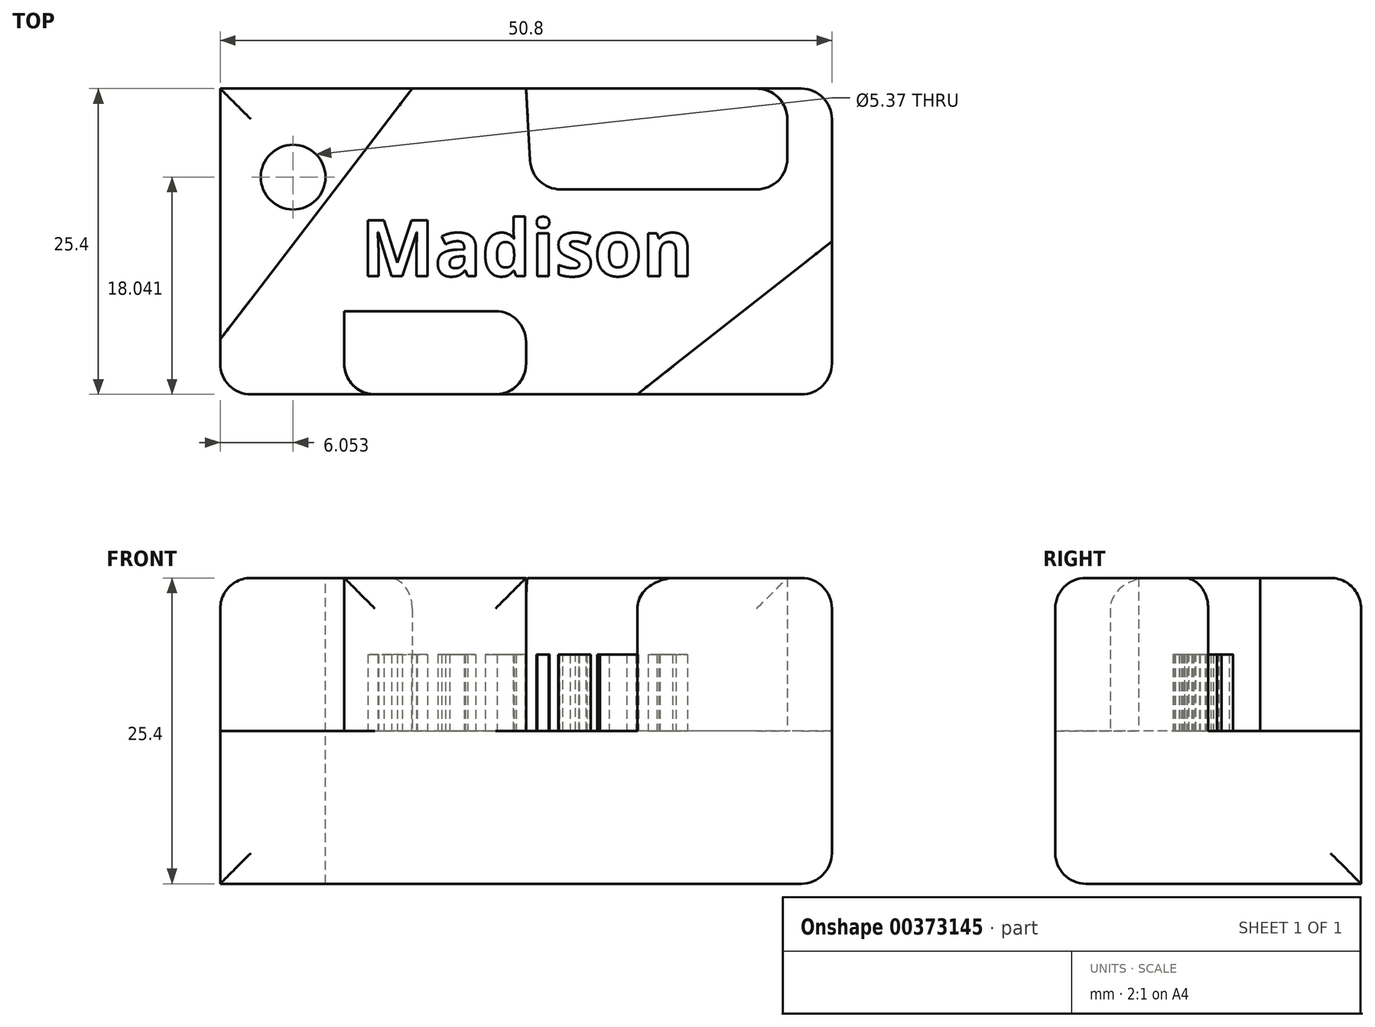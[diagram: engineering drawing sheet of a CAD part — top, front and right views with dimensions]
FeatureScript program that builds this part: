
annotation { "Feature Type Name" : "Feature", "Feature Type Description" : "" }
export const myFeature = defineFeature(function(context is Context, id is Id, definition is map)
    precondition{}
    {
        {
            var Q0;
            Q0=qCreatedBy(makeId("Front.planeOp"),FACE);
            var sketch = newSketch(context, id + "F0", { "sketchPlane" : qUnion([Q0])});
            skLineSegment(sketch, "E0", {"start": v(0, 12.7) * mm, "end": v(0, 0) * mm});
            skLineSegment(sketch, "E1", {"start": v(0, 0) * mm, "end": v(50.8, 0) * mm});
            skLineSegment(sketch, "E2", {"start": v(50.8, 0) * mm, "end": v(50.8, 12.7) * mm});
            skLineSegment(sketch, "E3", {"start": v(50.8, 12.7) * mm, "end": v(0, 12.7) * mm});
            skSolve(sketch);
        }
        {
            var Q0;
            Q0 = qSketchRegion(id + "F0", true);
            extrude(context, id + "F1", {"entities" : qUnion([Q0]), "depth" : 25.4 * mm});
        }
        {
            var Q0;
            Q0=makeQuery(id+"F1.opExtrude","SWEPT_FACE",FACE,{"disambiguationData":[OSD([sQuery(id+"F0.wireOp",EDGE,"E3")])]});
            var sketch = newSketch(context, id + "F2", { "sketchPlane" : qUnion([Q0])});
            skLineSegment(sketch, "E4", {"start": v(0, -20.83) * mm, "end": v(0, 0) * mm});
            skLineSegment(sketch, "E5", {"start": v(0, 0) * mm, "end": v(15.94, 0) * mm});
            skLineSegment(sketch, "E6", {"start": v(15.94, 0) * mm, "end": v(0, -20.83) * mm});
            skLineSegment(sketch, "E7", {"start": v(25.4, 0) * mm, "end": v(47.1, 0) * mm});
            skLineSegment(sketch, "E8", {"start": v(47.1, 0) * mm, "end": v(47.1, -8.37) * mm});
            skLineSegment(sketch, "E9", {"start": v(47.1, -8.37) * mm, "end": v(25.87, -8.37) * mm});
            skLineSegment(sketch, "E10", {"start": v(25.87, -8.37) * mm, "end": v(25.4, 0) * mm});
            skLineSegment(sketch, "E11", {"start": v(34.63, -25.4) * mm, "end": v(50.8, -25.4) * mm});
            skLineSegment(sketch, "E12", {"start": v(50.8, -25.4) * mm, "end": v(50.8, -12.7) * mm});
            skLineSegment(sketch, "E13", {"start": v(50.8, -12.7) * mm, "end": v(34.63, -25.4) * mm});
            skLineSegment(sketch, "E14", {"start": v(10.3, -25.4) * mm, "end": v(10.3, -18.5) * mm});
            skLineSegment(sketch, "E15", {"start": v(10.3, -18.5) * mm, "end": v(25.4, -18.5) * mm});
            skLineSegment(sketch, "E16", {"start": v(25.4, -18.5) * mm, "end": v(25.4, -25.4) * mm});
            skLineSegment(sketch, "E17", {"start": v(25.4, -25.4) * mm, "end": v(10.3, -25.4) * mm});
            skSolve(sketch);
        }
        {
            var Q0;
            Q0 = qSketchRegion(id + "F2", true);
            extrude(context, id + "F3", {"entities" : qUnion([Q0]), "operationType" : NewBodyOperationType.ADD, "depth" : 12.7 * mm});
        }
        {
            var Q0;
            Q0=makeQuery(id+"F3.opExtrude","CAP_EDGE",EDGE,{"disambiguationData":[OSD([sQuery(id+"F2.wireOp",EDGE,"E4")])],"isStart":false});
            var Q1;
            Q1=makeQuery(id+"F3.opExtrude","CAP_EDGE",EDGE,{"disambiguationData":[OSD([sQuery(id+"F2.wireOp",EDGE,"E5")])],"isStart":false});
            var Q2;
            Q2=makeQuery(id+"F3.opExtrude","CAP_EDGE",EDGE,{"disambiguationData":[OSD([sQuery(id+"F2.wireOp",EDGE,"E7")])],"isStart":false});
            var Q3;
            Q3=makeQuery(id+"F3.opExtrude","CAP_EDGE",EDGE,{"disambiguationData":[OSD([sQuery(id+"F2.wireOp",EDGE,"E17")])],"isStart":false});
            var Q4;
            Q4=makeQuery(id+"F3.opExtrude","CAP_EDGE",EDGE,{"disambiguationData":[OSD([sQuery(id+"F2.wireOp",EDGE,"E11")])],"isStart":false});
            var Q5;
            Q5=makeQuery(id+"F3.opExtrude","CAP_EDGE",EDGE,{"disambiguationData":[OSD([sQuery(id+"F2.wireOp",EDGE,"E12")])],"isStart":false});
            var Q6;
            Q6=makeQuery(id+"F1.opExtrude","SWEPT_EDGE",EDGE,{"disambiguationData":[OSD([sQuery(id+"F0.wireOp",EDGE,"E1"),sQuery(id+"F0.wireOp",EDGE,"E2")])]});
            var Q7;
            Q7=makeQuery(id+"F1.opExtrude","CAP_EDGE",EDGE,{"disambiguationData":[OSD([sQuery(id+"F0.wireOp",EDGE,"E1")])],"isStart":false});
            var Q8;
            Q8=makeQuery(id+"F3.boolean.opBoolean","MERGE",EDGE,{"derivedFrom":[makeQuery(id+"F1.opExtrude","CAP_EDGE",EDGE,{"disambiguationData":[OSD([sQuery(id+"F0.wireOp",EDGE,"E2")])],"isStart":false}),makeQuery(id+"F3.opExtrude","SWEPT_EDGE",EDGE,{"disambiguationData":[OSD([sQuery(id+"F2.wireOp",EDGE,"E11"),sQuery(id+"F2.wireOp",EDGE,"E12")])]})]});
            var Q9;
            Q9=makeQuery(id+"F1.opExtrude","CAP_EDGE",EDGE,{"disambiguationData":[OSD([sQuery(id+"F0.wireOp",EDGE,"E2")])],"isStart":true});
            var Q10;
            Q10=makeQuery(id+"F1.opExtrude","CAP_EDGE",EDGE,{"disambiguationData":[OSD([sQuery(id+"F0.wireOp",EDGE,"E0")])],"isStart":false});
            var Q11;
            Q11=makeQuery(id+"F3.opExtrude","SWEPT_EDGE",EDGE,{"disambiguationData":[OSD([sQuery(id+"F0.wireOp",EDGE,"E3"),sQuery(id+"F2.wireOp",EDGE,"E7"),sQuery(id+"F2.wireOp",EDGE,"E8")])]});
            var Q12;
            Q12=makeQuery(id+"F3.opExtrude","SWEPT_EDGE",EDGE,{"disambiguationData":[OSD([sQuery(id+"F0.wireOp",EDGE,"E3"),sQuery(id+"F2.wireOp",EDGE,"E16"),sQuery(id+"F2.wireOp",EDGE,"E17")])]});
            var Q13;
            Q13=makeQuery(id+"F3.opExtrude","SWEPT_EDGE",EDGE,{"disambiguationData":[OSD([sQuery(id+"F0.wireOp",EDGE,"E3"),sQuery(id+"F2.wireOp",EDGE,"E14"),sQuery(id+"F2.wireOp",EDGE,"E17")])]});
            var Q14;
            Q14=makeQuery(id+"F3.opExtrude","SWEPT_EDGE",EDGE,{"disambiguationData":[OSD([sQuery(id+"F2.wireOp",EDGE,"E8"),sQuery(id+"F2.wireOp",EDGE,"E9")])]});
            var Q15;
            Q15=makeQuery(id+"F3.opExtrude","SWEPT_EDGE",EDGE,{"disambiguationData":[OSD([sQuery(id+"F2.wireOp",EDGE,"E9"),sQuery(id+"F2.wireOp",EDGE,"E10")])]});
            var Q16;
            Q16=makeQuery(id+"F3.opExtrude","SWEPT_EDGE",EDGE,{"disambiguationData":[OSD([sQuery(id+"F2.wireOp",EDGE,"E15"),sQuery(id+"F2.wireOp",EDGE,"E16")])]});
            fillet(context, id + "F4", {"entities" : qUnion([Q0, Q1, Q2, Q3, Q4, Q5, Q6, Q7, Q8, Q9, Q10, Q11, Q12, Q13, Q14, Q15, Q16]), "radius" : 2.54 * mm, "tangentPropagation" : true, "allowEdgeOverflow" : false});
        }
        {
            var Q0;
            Q0=makeQuery(id+"F1.opExtrude","SWEPT_FACE",FACE,{"disambiguationData":[OSD([sQuery(id+"F0.wireOp",EDGE,"E3")])]});
            var sketch = newSketch(context, id + "F5", { "sketchPlane" : qUnion([Q0])});
            skText(sketch, "E18", { "text": "Madison", "fontName": "OpenSans-Bold.ttf"});
            const initialGuessF5  = {"E18": [0.01168, -0.01557, 1, 0, 0.00467]};
            skSetInitialGuess(sketch, initialGuessF5);
            skSolve(sketch);
        }
        {
            var Q0;
            Q0 = qSketchRegion(id + "F5", true);
            extrude(context, id + "F6", {"entities" : qUnion([Q0]), "operationType" : NewBodyOperationType.ADD, "depth" : 6.35 * mm});
        }
        {
            var Q0;
            Q0=makeQuery(id+"F3.opExtrude","CAP_FACE",FACE,{"disambiguationData":[OSD([sQuery(id+"F2.wireOp",EDGE,"E4"),sQuery(id+"F2.wireOp",EDGE,"E5"),sQuery(id+"F2.wireOp",EDGE,"E6")])],"isStart":false});
            var sketch = newSketch(context, id + "F7", { "sketchPlane" : qUnion([Q0])});
            skCircle(sketch, "E19", {"center": v(6.05, -7.36) * mm, "radius": 2.69 * mm});
            skPoint(sketch, "E19.first.point", {"position": v(6.12, -4.67) * mm});
            skPoint(sketch, "E19.second.point", {"position": v(5.73, -10.03) * mm});
            skPoint(sketch, "E19.second.point.positionSnap0", {"position": v(8.27, -10.03) * mm});
            skPoint(sketch, "E19.third.point", {"position": v(8.27, -5.84) * mm});
            skPoint(sketch, "E19.third.point.positionSnap0", {"position": v(8.27, -10.03) * mm});
            skSolve(sketch);
        }
        {
            var Q0;
            Q0=makeQuery(id+"F7.imprint","IMPRINT",FACE,{"disambiguationData":[TD([[makeQuery(id+"F7.imprint","IMPRINT",EDGE,{"derivedFrom":sQuery(id+"F7.wireOp",EDGE,"E19")}),1.0]])]});
            extrude(context, id + "F8", {"entities" : qUnion([Q0]), "operationType" : NewBodyOperationType.REMOVE, "oppositeDirection" : true, "depth" : 25.4 * mm});
        }
    });
